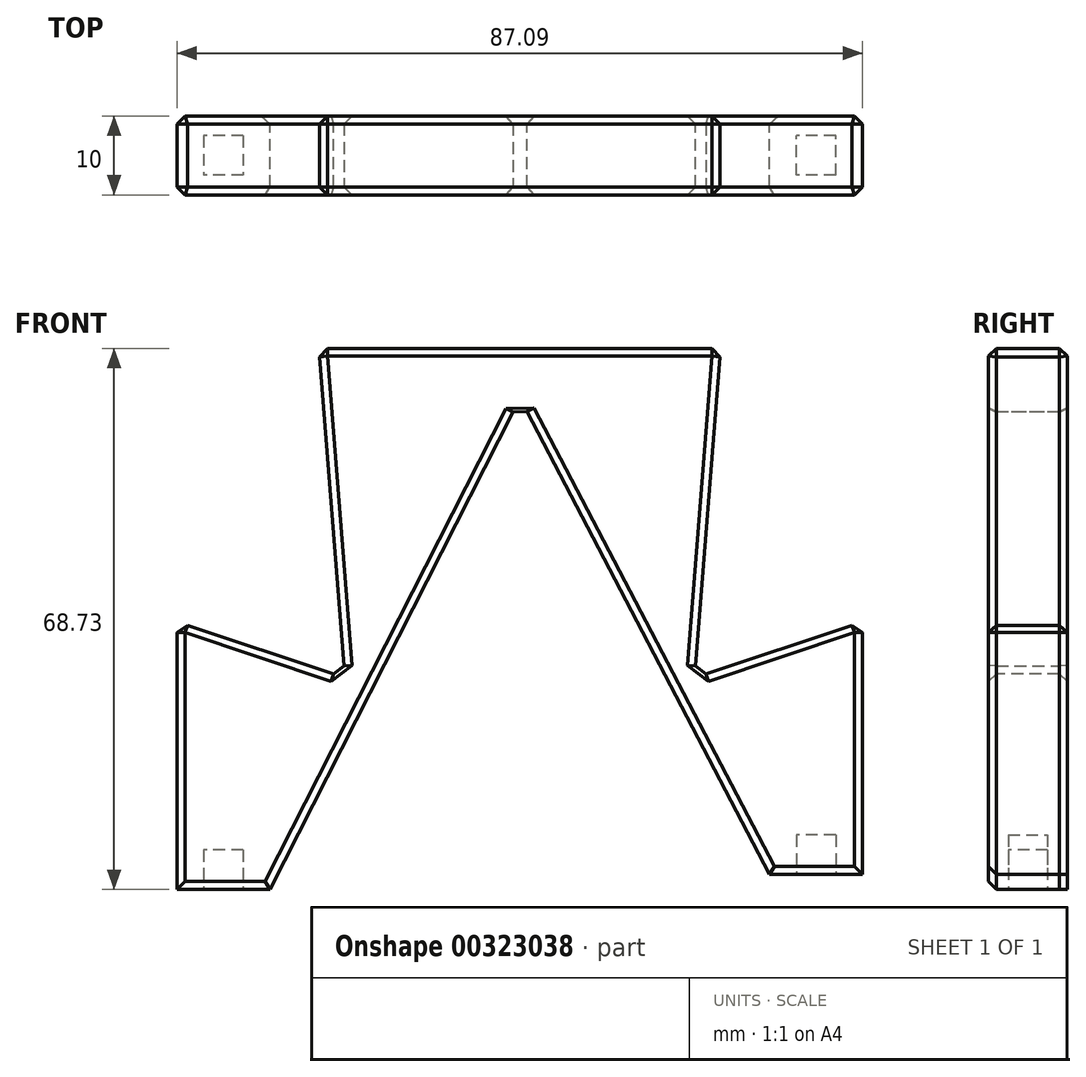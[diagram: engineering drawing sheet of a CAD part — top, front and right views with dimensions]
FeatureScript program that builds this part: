
annotation { "Feature Type Name" : "Feature", "Feature Type Description" : "" }
export const myFeature = defineFeature(function(context is Context, id is Id, definition is map)
    precondition{}
    {
        {
            var Q0;
            Q0=qCreatedBy(makeId("Front.planeOp"),FACE);
            var sketch = newSketch(context, id + "F0", { "sketchPlane" : qUnion([Q0])});
            skLineSegment(sketch, "E0", {"start": v(21.34, 0) * mm, "end": v(9.54, 0) * mm});
            skLineSegment(sketch, "E1", {"start": v(21.34, 32.1) * mm, "end": v(21.34, 0) * mm});
            skLineSegment(sketch, "E2", {"start": v(21.34, 32.1) * mm, "end": v(0, 24.96) * mm});
            skLineSegment(sketch, "E3", {"start": v(3.3, 66.83) * mm, "end": v(0, 24.96) * mm});
            skLineSegment(sketch, "E4", {"start": v(-47.7, 66.83) * mm, "end": v(3.3, 66.83) * mm});
            skLineSegment(sketch, "E5", {"start": v(-22.2, 66.83) * mm, "end": v(-22.2, 60.49) * mm});
            skLineSegment(sketch, "E6", {"start": v(-44.4, 24.96) * mm, "end": v(-47.7, 66.83) * mm});
            skLineSegment(sketch, "E7", {"start": v(-44.4, 24.96) * mm, "end": v(-65.75, 32.1) * mm});
            skLineSegment(sketch, "E8", {"start": v(-65.75, 32.1) * mm, "end": v(-65.75, -1.9) * mm});
            skLineSegment(sketch, "E9", {"start": v(-53.95, -1.9) * mm, "end": v(-65.75, -1.9) * mm});
            skLineSegment(sketch, "E10", {"start": v(-53.95, -1.9) * mm, "end": v(-22.2, 60.49) * mm});
            skLineSegment(sketch, "E11", {"start": v(-22.2, 60.49) * mm, "end": v(9.54, 0) * mm});
            skSolve(sketch);
        }
        {
            var Q0;
            {var subQ1=sQuery(id+"F0.wireOp",EDGE,"E5");Q0=makeQuery(id+"F0.imprint","IMPRINT",FACE,{"disambiguationData":[TD([[makeQuery(id+"F0.imprint","IMPRINT",EDGE,{"derivedFrom":subQ1}),-1.0]])]});}
            var Q1;
            Q1=makeQuery(id+"F0.imprint","IMPRINT",FACE,{"disambiguationData":[TD([[makeQuery(id+"F0.imprint","IMPRINT",EDGE,{"derivedFrom":sQuery(id+"F0.wireOp",EDGE,"E0")}),-1.0]])]});
            extrude(context, id + "F1", {"entities" : qUnion([Q0, Q1]), "depth" : 10 * mm});
        }
        {
            var Q0;
            Q0=makeQuery(id+"F1.opExtrude","SWEPT_FACE",FACE,{"disambiguationData":[OSD([sQuery(id+"F0.wireOp",EDGE,"E9")])]});
            var sketch = newSketch(context, id + "F2", { "sketchPlane" : qUnion([Q0])});
            skLineSegment(sketch, "E12", {"start": v(-59.85, 10) * mm, "end": v(-59.85, 0) * mm});
            skLineSegment(sketch, "E13", {"start": v(-65.75, 5) * mm, "end": v(-53.95, 5) * mm});
            skPoint(sketch, "E14", {"position": v(-59.85, 5) * mm});
            skLineSegment(sketch, "E15.bottom", {"start": v(-57.35, 2.5) * mm, "end": v(-62.35, 2.5) * mm});
            skLineSegment(sketch, "E15.top", {"start": v(-57.35, 7.5) * mm, "end": v(-62.35, 7.5) * mm});
            skLineSegment(sketch, "E15.left", {"start": v(-57.35, 2.5) * mm, "end": v(-57.35, 7.5) * mm});
            skLineSegment(sketch, "E15.right", {"start": v(-62.35, 2.5) * mm, "end": v(-62.35, 7.5) * mm});
            skSolve(sketch);
        }
        {
            var Q0;
            {var subQ0=sQuery(id+"F2.wireOp",EDGE,"E13");var subQ1=sQuery(id+"F2.wireOp",EDGE,"E12");var subQ2=makeQuery(id+"F2.imprint","INTERSECT",VERTEX,{"derivedFrom":[subQ1,subQ0]});Q0=makeQuery(id+"F2.imprint","IMPRINT",FACE,{"disambiguationData":[TD([[makeQuery(id+"F2.imprint","IMPRINT",EDGE,{"disambiguationData":[TD([[subQ2,-1.0]])],"derivedFrom":subQ1}),1.0]])]});}
            var Q1;
            {var subQ0=sQuery(id+"F2.wireOp",EDGE,"E15.top");var subQ1=sQuery(id+"F2.wireOp",EDGE,"E12");var subQ2=makeQuery(id+"F2.imprint","INTERSECT",VERTEX,{"derivedFrom":[subQ1,subQ0]});Q1=makeQuery(id+"F2.imprint","IMPRINT",FACE,{"disambiguationData":[TD([[makeQuery(id+"F2.imprint","IMPRINT",EDGE,{"disambiguationData":[TD([[subQ2,-1.0]])],"derivedFrom":subQ1}),-1.0]])]});}
            var Q2;
            {var subQ0=sQuery(id+"F2.wireOp",EDGE,"E13");var subQ1=sQuery(id+"F2.wireOp",EDGE,"E12");var subQ2=makeQuery(id+"F2.imprint","INTERSECT",VERTEX,{"derivedFrom":[subQ1,subQ0]});Q2=makeQuery(id+"F2.imprint","IMPRINT",FACE,{"disambiguationData":[TD([[makeQuery(id+"F2.imprint","IMPRINT",EDGE,{"disambiguationData":[TD([[subQ2,-1.0]])],"derivedFrom":subQ1}),-1.0]])]});}
            var Q3;
            {var subQ0=sQuery(id+"F2.wireOp",EDGE,"E15.top");var subQ1=sQuery(id+"F2.wireOp",EDGE,"E12");var subQ2=makeQuery(id+"F2.imprint","INTERSECT",VERTEX,{"derivedFrom":[subQ1,subQ0]});Q3=makeQuery(id+"F2.imprint","IMPRINT",FACE,{"disambiguationData":[TD([[makeQuery(id+"F2.imprint","IMPRINT",EDGE,{"disambiguationData":[TD([[subQ2,-1.0]])],"derivedFrom":subQ1}),1.0]])]});}
            extrude(context, id + "F3", {"entities" : qUnion([Q0, Q1, Q2, Q3]), "operationType" : NewBodyOperationType.REMOVE, "oppositeDirection" : true, "depth" : 5 * mm});
        }
        {
            var Q0;
            Q0=makeQuery(id+"F1.opExtrude","SWEPT_FACE",FACE,{"disambiguationData":[OSD([sQuery(id+"F0.wireOp",EDGE,"E0")])]});
            var sketch = newSketch(context, id + "F4", { "sketchPlane" : qUnion([Q0])});
            skLineSegment(sketch, "E16", {"start": v(15.44, 10) * mm, "end": v(15.44, 0) * mm});
            skLineSegment(sketch, "E17", {"start": v(9.54, 5) * mm, "end": v(21.34, 5) * mm});
            skPoint(sketch, "E18", {"position": v(15.44, 5) * mm});
            skLineSegment(sketch, "E19.bottom", {"start": v(17.94, 7.5) * mm, "end": v(12.94, 7.5) * mm});
            skLineSegment(sketch, "E19.top", {"start": v(17.94, 2.5) * mm, "end": v(12.94, 2.5) * mm});
            skLineSegment(sketch, "E19.left", {"start": v(17.94, 7.5) * mm, "end": v(17.94, 2.5) * mm});
            skLineSegment(sketch, "E19.right", {"start": v(12.94, 7.5) * mm, "end": v(12.94, 2.5) * mm});
            skSolve(sketch);
        }
        {
            var Q0;
            Q0 = qSketchRegion(id + "F4", true);
            extrude(context, id + "F5", {"entities" : qUnion([Q0]), "operationType" : NewBodyOperationType.REMOVE, "oppositeDirection" : true, "depth" : 5 * mm});
        }
        {
            var Q0;
            Q0=makeQuery(id+"F1.opExtrude","CAP_EDGE",EDGE,{"disambiguationData":[OSD([sQuery(id+"F0.wireOp",EDGE,"E10")])],"isStart":false});
            var Q1;
            Q1=makeQuery(id+"F1.opExtrude","CAP_EDGE",EDGE,{"disambiguationData":[OSD([sQuery(id+"F0.wireOp",EDGE,"E11")])],"isStart":false});
            var Q2;
            Q2=makeQuery(id+"F1.opExtrude","CAP_EDGE",EDGE,{"disambiguationData":[OSD([sQuery(id+"F0.wireOp",EDGE,"E3")])],"isStart":false});
            var Q3;
            Q3=makeQuery(id+"F1.opExtrude","CAP_EDGE",EDGE,{"disambiguationData":[OSD([sQuery(id+"F0.wireOp",EDGE,"E2")])],"isStart":false});
            var Q4;
            Q4=makeQuery(id+"F1.opExtrude","CAP_EDGE",EDGE,{"disambiguationData":[OSD([sQuery(id+"F0.wireOp",EDGE,"E1")])],"isStart":false});
            var Q5;
            Q5=makeQuery(id+"F1.opExtrude","CAP_EDGE",EDGE,{"disambiguationData":[OSD([sQuery(id+"F0.wireOp",EDGE,"E4")])],"isStart":false});
            var Q6;
            Q6=makeQuery(id+"F1.opExtrude","CAP_EDGE",EDGE,{"disambiguationData":[OSD([sQuery(id+"F0.wireOp",EDGE,"E6")])],"isStart":false});
            var Q7;
            Q7=makeQuery(id+"F1.opExtrude","CAP_EDGE",EDGE,{"disambiguationData":[OSD([sQuery(id+"F0.wireOp",EDGE,"E7")])],"isStart":false});
            var Q8;
            Q8=makeQuery(id+"F1.opExtrude","CAP_FACE",FACE,{"disambiguationData":[OSD([sQuery(id+"F0.wireOp",EDGE,"E0"),sQuery(id+"F0.wireOp",EDGE,"E1"),sQuery(id+"F0.wireOp",EDGE,"E2"),sQuery(id+"F0.wireOp",EDGE,"E3"),sQuery(id+"F0.wireOp",EDGE,"E4"),sQuery(id+"F0.wireOp",EDGE,"E6"),sQuery(id+"F0.wireOp",EDGE,"E7"),sQuery(id+"F0.wireOp",EDGE,"E8"),sQuery(id+"F0.wireOp",EDGE,"E9"),sQuery(id+"F0.wireOp",EDGE,"E10"),sQuery(id+"F0.wireOp",EDGE,"E11")])],"isStart":false});
            var Q9;
            Q9=makeQuery(id+"F1.opExtrude","CAP_EDGE",EDGE,{"disambiguationData":[OSD([sQuery(id+"F0.wireOp",EDGE,"E1")])],"isStart":true});
            var Q10;
            Q10=makeQuery(id+"F1.opExtrude","CAP_EDGE",EDGE,{"disambiguationData":[OSD([sQuery(id+"F0.wireOp",EDGE,"E2")])],"isStart":true});
            var Q11;
            Q11=makeQuery(id+"F1.opExtrude","CAP_EDGE",EDGE,{"disambiguationData":[OSD([sQuery(id+"F0.wireOp",EDGE,"E11")])],"isStart":true});
            var Q12;
            Q12=makeQuery(id+"F1.opExtrude","CAP_EDGE",EDGE,{"disambiguationData":[OSD([sQuery(id+"F0.wireOp",EDGE,"E3")])],"isStart":true});
            var Q13;
            Q13=makeQuery(id+"F1.opExtrude","CAP_EDGE",EDGE,{"disambiguationData":[OSD([sQuery(id+"F0.wireOp",EDGE,"E4")])],"isStart":true});
            var Q14;
            Q14=makeQuery(id+"F1.opExtrude","CAP_EDGE",EDGE,{"disambiguationData":[OSD([sQuery(id+"F0.wireOp",EDGE,"E6")])],"isStart":true});
            var Q15;
            Q15=makeQuery(id+"F1.opExtrude","CAP_EDGE",EDGE,{"disambiguationData":[OSD([sQuery(id+"F0.wireOp",EDGE,"E7")])],"isStart":true});
            var Q16;
            Q16=makeQuery(id+"F1.opExtrude","CAP_EDGE",EDGE,{"disambiguationData":[OSD([sQuery(id+"F0.wireOp",EDGE,"E8")])],"isStart":true});
            var Q17;
            Q17=makeQuery(id+"F1.opExtrude","CAP_EDGE",EDGE,{"disambiguationData":[OSD([sQuery(id+"F0.wireOp",EDGE,"E10")])],"isStart":true});
            var Q18;
            Q18=makeQuery(id+"F1.opExtrude","SWEPT_FACE",FACE,{"disambiguationData":[OSD([sQuery(id+"F0.wireOp",EDGE,"E4")])]});
            var Q19;
            Q19=makeQuery(id+"F1.opExtrude","SWEPT_FACE",FACE,{"disambiguationData":[OSD([sQuery(id+"F0.wireOp",EDGE,"E2")])]});
            var Q20;
            Q20=makeQuery(id+"F1.opExtrude","SWEPT_FACE",FACE,{"disambiguationData":[OSD([sQuery(id+"F0.wireOp",EDGE,"E7")])]});
            var Q21;
            Q21=makeQuery(id+"F1.opExtrude","SWEPT_EDGE",EDGE,{"disambiguationData":[OSD([sQuery(id+"F0.wireOp",EDGE,"E5"),sQuery(id+"F0.wireOp",EDGE,"E10"),sQuery(id+"F0.wireOp",EDGE,"E11")])]});
            chamfer(context, id + "F6", {"entities" : qUnion([Q0, Q1, Q2, Q3, Q4, Q5, Q6, Q7, Q8, Q9, Q10, Q11, Q12, Q13, Q14, Q15, Q16, Q17, Q18, Q19, Q20, Q21]), "width" : 1 * mm, "tangentPropagation" : true});
        }
    });
